# Revit family: Specialty_Equipment-Fiberglass_Planter-Planters_Unlimited-Nazca-Square
name_source: partatom
category: Specialty Equipment
units: mm (PartAtom-declared; Revit-internal decimal feet)

## family parameters
Always vertical = Yes
Cut with Voids When Loaded = No
Enable Cutting in Views = No
Maintain Annotation Orientation = No
OmniClass Number = 23.40.05.21.17
OmniClass Title = Planters
Part Type = Normal
Room Calculation Point = No
Round Connector Dimension = Use Diameter
Shared = No
Work Plane-Based = No

## types (72) — shared parameters
Assembly Code = G2050600
CD_Cut angle = 12.72°
CD_Finish = Plastic-Fiberglass-Carlsbad-Semi_Gloss-Charcoal
CD_Microsite = https://www.caddetails.com
CD_Product Page URL = https://www.plantersunlimited.com
CD_Specification = https://www.plantersunlimited.com
Default Elevation = 0.0"
Description = Nazca Square Planter
Manufacturer = Planters Unlimited
Model = Nazca Series Planter
Type Comments = Square Planter
URL = https://www.plantersunlimited.com

## per-type parameters (varying)
| type | CD_Base Length | CD_Height | CD_Length | CD_Lip Width | CD_Pad Spacing | CD_Top Lip | CD_Width |
| 18"L x 18"W x 18"H | 6.0" | 18.0" | 18.0" | 15.0" | 4.0" | 4.5" | 18.0" |
| 18"L x 18"W x 24"H | 6.0" | 24.0" | 18.0" | 15.0" | 4.0" | 4.5" | 18.0" |
| 18"L x 18"W x 30"H | 6.0" | 30.0" | 18.0" | 15.0" | 4.0" | 4.5" | 18.0" |
| 18"L x 18"W x 36"H | 6.0" | 36.0" | 18.0" | 15.0" | 4.0" | 4.5" | 18.0" |
| 18"L x 18"W x 42"H | 6.0" | 42.0" | 18.0" | 15.0" | 4.0" | 4.5" | 18.0" |
| 18"L x 18"W x 48"H | 6.0" | 48.0" | 18.0" | 15.0" | 4.0" | 4.5" | 18.0" |
| 18"L x 18"W x 54"H | 6.0" | 54.0" | 18.0" | 15.0" | 4.0" | 4.5" | 18.0" |
| 18"L x 18"W x 60"H | 6.0" | 60.0" | 18.0" | 15.0" | 4.0" | 4.5" | 18.0" |
| 24"L x 24"W x 18"H | 8.0" | 18.0" | 24.0" | 21.0" | 6.0" | 6.0" | 24.0" |
| 24"L x 24"W x 24"H | 8.0" | 24.0" | 24.0" | 21.0" | 6.0" | 6.0" | 24.0" |
| 24"L x 24"W x 30"H | 8.0" | 30.0" | 24.0" | 21.0" | 6.0" | 6.0" | 24.0" |
| 24"L x 24"W x 36"H | 8.0" | 36.0" | 24.0" | 21.0" | 6.0" | 6.0" | 24.0" |
| 24"L x 24"W x 42"H | 8.0" | 42.0" | 24.0" | 21.0" | 6.0" | 6.0" | 24.0" |
| 24"L x 24"W x 48"H | 8.0" | 48.0" | 24.0" | 21.0" | 6.0" | 6.0" | 24.0" |
| 24"L x 24"W x 54"H | 8.0" | 54.0" | 24.0" | 21.0" | 6.0" | 6.0" | 24.0" |
| 24"L x 24"W x 60"H | 8.0" | 60.0" | 24.0" | 21.0" | 6.0" | 6.0" | 24.0" |
| 30"L x 30"W x 18"H | 10.0" | 18.0" | 30.0" | 27.0" | 8.0" | 7.5" | 30.0" |
| 30"L x 30"W x 24"H | 10.0" | 24.0" | 30.0" | 27.0" | 8.0" | 7.5" | 30.0" |
| 30"L x 30"W x 30"H | 10.0" | 30.0" | 30.0" | 27.0" | 8.0" | 7.5" | 30.0" |
| 30"L x 30"W x 36"H | 10.0" | 36.0" | 30.0" | 27.0" | 8.0" | 7.5" | 30.0" |
| 30"L x 30"W x 42"H | 10.0" | 42.0" | 30.0" | 27.0" | 8.0" | 7.5" | 30.0" |
| 30"L x 30"W x 48"H | 10.0" | 48.0" | 30.0" | 27.0" | 8.0" | 7.5" | 30.0" |
| 30"L x 30"W x 54"H | 10.0" | 54.0" | 30.0" | 27.0" | 8.0" | 7.5" | 30.0" |
| 30"L x 30"W x 60"H | 10.0" | 60.0" | 30.0" | 27.0" | 8.0" | 7.5" | 30.0" |
| 36"L x 36"W x 18"H | 12.0" | 18.0" | 36.0" | 33.0" | 10.0" | 9.0" | 36.0" |
| 36"L x 36"W x 24"H | 12.0" | 24.0" | 36.0" | 33.0" | 10.0" | 9.0" | 36.0" |
| 36"L x 36"W x 30"H | 12.0" | 30.0" | 36.0" | 33.0" | 10.0" | 9.0" | 36.0" |
| 36"L x 36"W x 36"H | 12.0" | 36.0" | 36.0" | 33.0" | 10.0" | 9.0" | 36.0" |
| 36"L x 36"W x 42"H | 12.0" | 42.0" | 36.0" | 33.0" | 10.0" | 9.0" | 36.0" |
| 36"L x 36"W x 48"H | 12.0" | 48.0" | 36.0" | 33.0" | 10.0" | 9.0" | 36.0" |
| 36"L x 36"W x 54"H | 12.0" | 54.0" | 36.0" | 33.0" | 10.0" | 9.0" | 36.0" |
| 36"L x 36"W x 60"H | 12.0" | 60.0" | 36.0" | 33.0" | 10.0" | 9.0" | 36.0" |
| 42"L x 42"W x 18"H | 14.0" | 18.0" | 42.0" | 39.0" | 12.0" | 10.5" | 42.0" |
| 42"L x 42"W x 24"H | 14.0" | 24.0" | 42.0" | 39.0" | 12.0" | 10.5" | 42.0" |
| 42"L x 42"W x 30"H | 14.0" | 30.0" | 42.0" | 39.0" | 12.0" | 10.5" | 42.0" |
| 42"L x 42"W x 36"H | 14.0" | 36.0" | 42.0" | 39.0" | 12.0" | 10.5" | 42.0" |
| 42"L x 42"W x 42"H | 14.0" | 42.0" | 42.0" | 39.0" | 12.0" | 10.5" | 42.0" |
| 42"L x 42"W x 48"H | 14.0" | 48.0" | 42.0" | 39.0" | 12.0" | 10.5" | 42.0" |
| 42"L x 42"W x 54"H | 14.0" | 54.0" | 42.0" | 39.0" | 12.0" | 10.5" | 42.0" |
| 42"L x 42"W x 60"H | 14.0" | 60.0" | 42.0" | 39.0" | 12.0" | 10.5" | 42.0" |
| 48"L x 48"W x 18"H | 16.0" | 18.0" | 48.0" | 45.0" | 14.0" | 12.0" | 48.0" |
| 48"L x 48"W x 24"H | 16.0" | 24.0" | 48.0" | 45.0" | 14.0" | 12.0" | 48.0" |
| 48"L x 48"W x 30"H | 16.0" | 30.0" | 48.0" | 45.0" | 14.0" | 12.0" | 48.0" |
| 48"L x 48"W x 36"H | 16.0" | 36.0" | 48.0" | 45.0" | 14.0" | 12.0" | 48.0" |
| 48"L x 48"W x 42"H | 16.0" | 42.0" | 48.0" | 45.0" | 14.0" | 12.0" | 48.0" |
| 48"L x 48"W x 48"H | 16.0" | 48.0" | 48.0" | 45.0" | 14.0" | 12.0" | 48.0" |
| 48"L x 48"W x 54"H | 16.0" | 54.0" | 48.0" | 45.0" | 14.0" | 12.0" | 48.0" |
| 48"L x 48"W x 60"H | 16.0" | 60.0" | 48.0" | 45.0" | 14.0" | 12.0" | 48.0" |
| 60"L x 60"W x 18"H | 20.0" | 18.0" | 60.0" | 57.0" | 18.0" | 15.0" | 60.0" |
| 60"L x 60"W x 24"H | 20.0" | 24.0" | 60.0" | 57.0" | 18.0" | 15.0" | 60.0" |
| 60"L x 60"W x 30"H | 20.0" | 30.0" | 60.0" | 57.0" | 18.0" | 15.0" | 60.0" |
| 60"L x 60"W x 36"H | 20.0" | 36.0" | 60.0" | 57.0" | 18.0" | 15.0" | 60.0" |
| 60"L x 60"W x 42"H | 20.0" | 42.0" | 60.0" | 57.0" | 18.0" | 15.0" | 60.0" |
| 60"L x 60"W x 48"H | 20.0" | 48.0" | 60.0" | 57.0" | 18.0" | 15.0" | 60.0" |
| 60"L x 60"W x 54"H | 20.0" | 54.0" | 60.0" | 57.0" | 18.0" | 15.0" | 60.0" |
| 60"L x 60"W x 60"H | 20.0" | 60.0" | 60.0" | 57.0" | 18.0" | 15.0" | 60.0" |
| 66"L x 66"W x 18"H | 22.0" | 18.0" | 66.0" | 63.0" | 20.0" | 16.5" | 66.0" |
| 66"L x 66"W x 24"H | 22.0" | 24.0" | 66.0" | 63.0" | 20.0" | 16.5" | 66.0" |
| 66"L x 66"W x 30"H | 22.0" | 30.0" | 66.0" | 63.0" | 20.0" | 16.5" | 66.0" |
| 66"L x 66"W x 36"H | 22.0" | 36.0" | 66.0" | 63.0" | 20.0" | 16.5" | 66.0" |
| 66"L x 66"W x 42"H | 22.0" | 42.0" | 66.0" | 63.0" | 20.0" | 16.5" | 66.0" |
| 66"L x 66"W x 48"H | 22.0" | 48.0" | 66.0" | 63.0" | 20.0" | 16.5" | 66.0" |
| 66"L x 66"W x 54"H | 22.0" | 54.0" | 66.0" | 63.0" | 20.0" | 16.5" | 66.0" |
| 66"L x 66"W x 60"H | 22.0" | 60.0" | 66.0" | 63.0" | 20.0" | 16.5" | 66.0" |
| 72"L x 72"W x 18"H | 24.0" | 18.0" | 72.0" | 69.0" | 22.0" | 18.0" | 72.0" |
| 72"L x 72"W x 24"H | 24.0" | 24.0" | 72.0" | 69.0" | 22.0" | 18.0" | 72.0" |
| 72"L x 72"W x 30"H | 24.0" | 30.0" | 72.0" | 69.0" | 22.0" | 18.0" | 72.0" |
| 72"L x 72"W x 36"H | 24.0" | 36.0" | 72.0" | 69.0" | 22.0" | 18.0" | 72.0" |
| 72"L x 72"W x 42"H | 24.0" | 42.0" | 72.0" | 69.0" | 22.0" | 18.0" | 72.0" |
| 72"L x 72"W x 48"H | 24.0" | 48.0" | 72.0" | 69.0" | 22.0" | 18.0" | 72.0" |
| 72"L x 72"W x 54"H | 24.0" | 54.0" | 72.0" | 69.0" | 22.0" | 18.0" | 72.0" |
| 72"L x 72"W x 60"H | 24.0" | 60.0" | 72.0" | 69.0" | 22.0" | 18.0" | 72.0" |

## geometry (parser evidence)
native form markers: Sweep x5
no freeform markers — native parametric forms only
